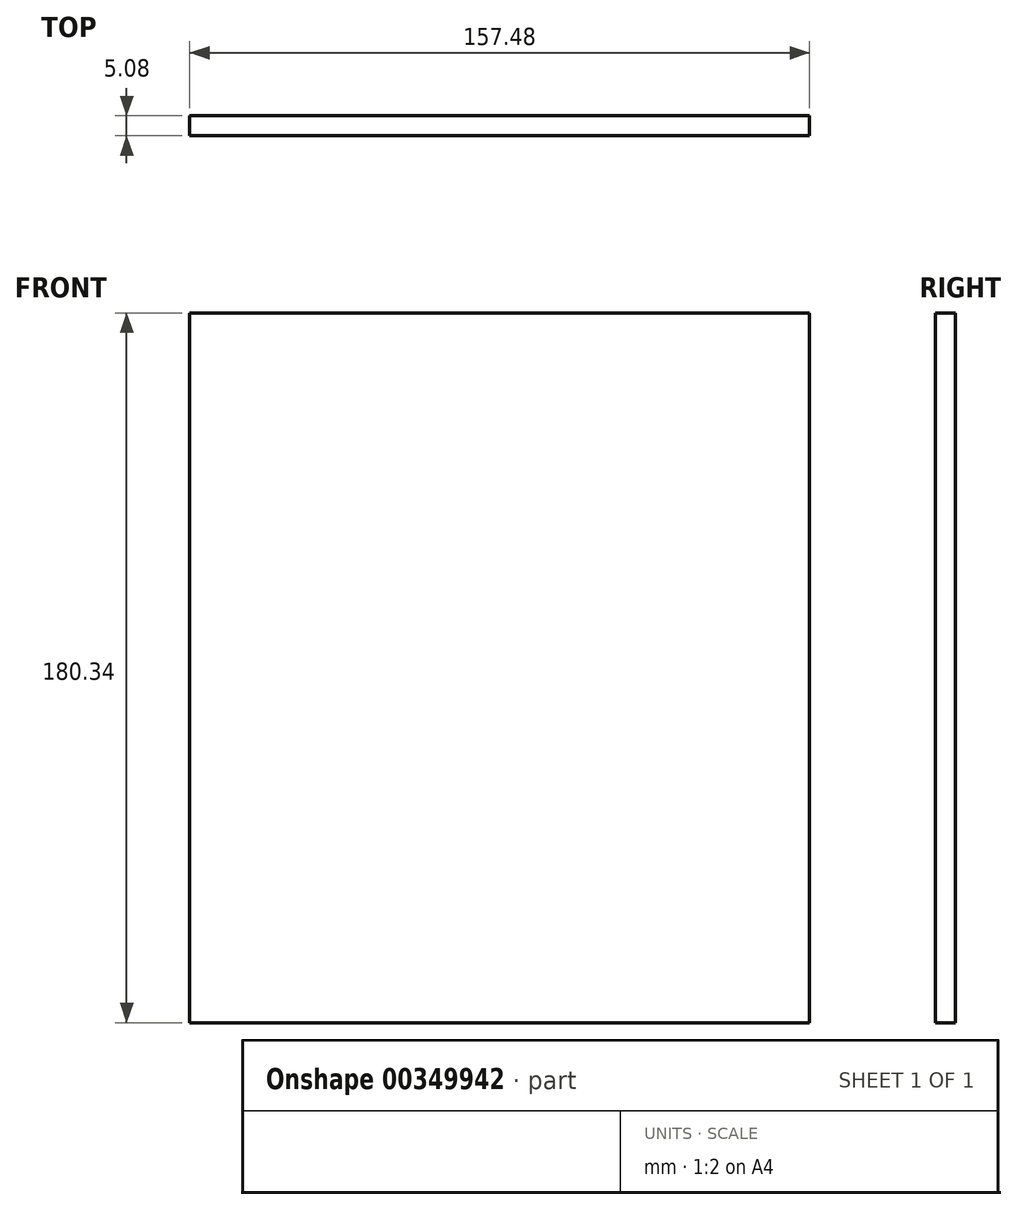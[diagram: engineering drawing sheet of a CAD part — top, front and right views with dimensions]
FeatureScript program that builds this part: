
annotation { "Feature Type Name" : "Feature", "Feature Type Description" : "" }
export const myFeature = defineFeature(function(context is Context, id is Id, definition is map)
    precondition{}
    {
        {
            var Q0;
            Q0=qCreatedBy(makeId("Front.planeOp"),FACE);
            var sketch = newSketch(context, id + "F0", { "sketchPlane" : qUnion([Q0])});
            skLineSegment(sketch, "E0.bottom", {"start": v(78.74, -90.17) * mm, "end": v(-78.74, -90.17) * mm});
            skLineSegment(sketch, "E0.top", {"start": v(78.74, 90.17) * mm, "end": v(-78.74, 90.17) * mm});
            skLineSegment(sketch, "E0.left", {"start": v(78.74, -90.17) * mm, "end": v(78.74, 90.17) * mm});
            skLineSegment(sketch, "E0.right", {"start": v(-78.74, -90.17) * mm, "end": v(-78.74, 90.17) * mm});
            skPoint(sketch, "E0.middle", {"position": v(0, 0) * mm});
            skSolve(sketch);
        }
        {
            var Q0;
            Q0 = qSketchRegion(id + "F0", true);
            extrude(context, id + "F1", {"entities" : qUnion([Q0]), "depth" : 5.08 * mm, "offsetDistance" : 25.4 * mm});
        }
    });
